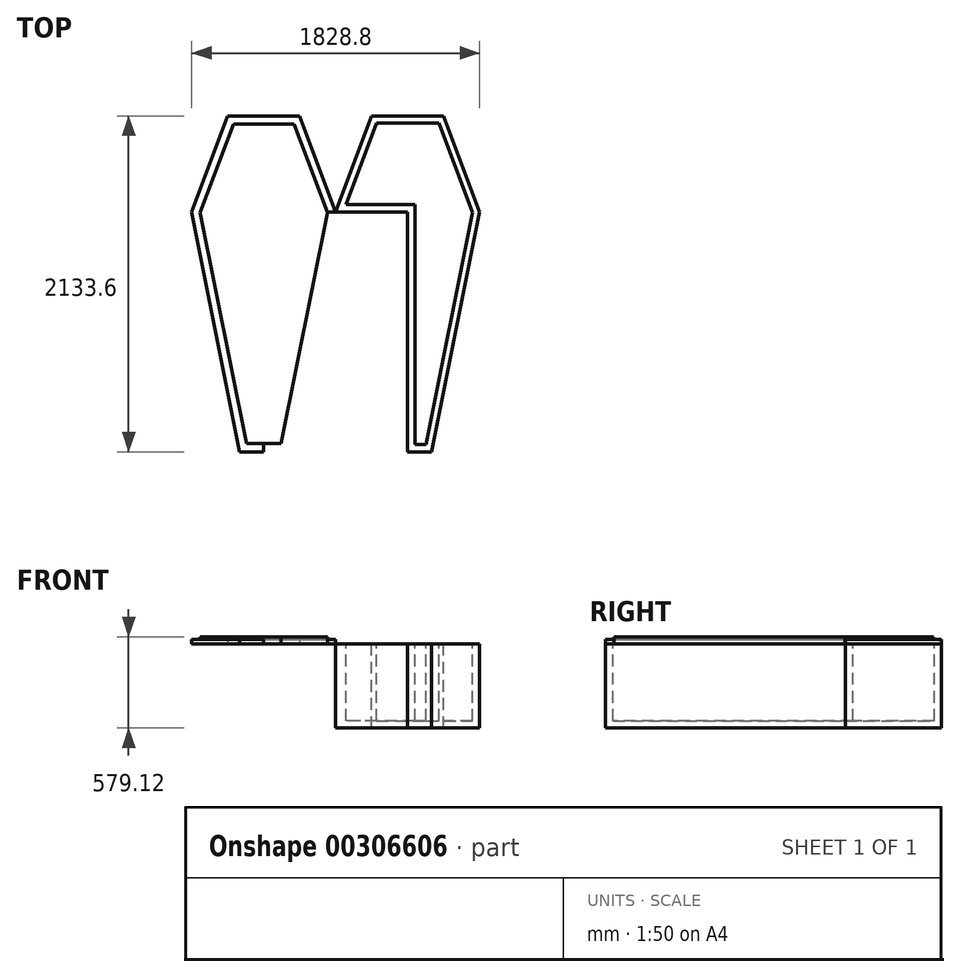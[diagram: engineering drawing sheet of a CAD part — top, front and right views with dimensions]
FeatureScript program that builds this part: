
annotation { "Feature Type Name" : "Feature", "Feature Type Description" : "" }
export const myFeature = defineFeature(function(context is Context, id is Id, definition is map)
    precondition{}
    {
        {
            var Q0;
            Q0=qCreatedBy(makeId("Top.planeOp"),FACE);
            var sketch = newSketch(context, id + "F0", { "sketchPlane" : qUnion([Q0])});
            skLineSegment(sketch, "E0", {"start": v(0, 0) * mm, "end": v(0, 609.6) * mm});
            skLineSegment(sketch, "E1", {"start": v(0, 0) * mm, "end": v(0, -1524) * mm});
            skLineSegment(sketch, "E2", {"start": v(0, 0) * mm, "end": v(-457.2, 0) * mm});
            skLineSegment(sketch, "E3", {"start": v(0, 0) * mm, "end": v(457.2, 0) * mm});
            skLineSegment(sketch, "E4", {"start": v(0, -1524) * mm, "end": v(152.4, -1524) * mm});
            skLineSegment(sketch, "E5", {"start": v(152.4, -1524) * mm, "end": v(0, -1524) * mm});
            skLineSegment(sketch, "E6", {"start": v(-152.4, -1524) * mm, "end": v(-457.2, 0) * mm});
            skLineSegment(sketch, "E7", {"start": v(-457.2, 0) * mm, "end": v(-228.6, 609.6) * mm});
            skLineSegment(sketch, "E8", {"start": v(-228.6, 609.6) * mm, "end": v(0, 609.6) * mm});
            skLineSegment(sketch, "E9", {"start": v(228.6, 609.6) * mm, "end": v(457.2, 0) * mm});
            skLineSegment(sketch, "E10", {"start": v(152.4, -1524) * mm, "end": v(457.2, 0) * mm});
            skLineSegment(sketch, "E11", {"start": v(228.6, 609.6) * mm, "end": v(0, 609.6) * mm});
            skLineSegment(sketch, "E12", {"start": v(-152.4, -1524) * mm, "end": v(0, -1524) * mm});
            skLineSegment(sketch, "E13", {"start": v(457.2, -1524) * mm, "end": v(457.2, 692.27) * mm, "construction": true});
            skLineSegment(sketch, "E14.MirrorCS", {"start": v(914.4, -1524) * mm, "end": v(762, -1524) * mm});
            skLineSegment(sketch, "E15.MirrorCS", {"start": v(762, -1524) * mm, "end": v(914.4, -1524) * mm});
            skLineSegment(sketch, "E16.MirrorCS", {"start": v(1066.8, -1524) * mm, "end": v(914.4, -1524) * mm});
            skLineSegment(sketch, "E17.MirrorCS", {"start": v(914.4, 0) * mm, "end": v(914.4, 609.6) * mm});
            skLineSegment(sketch, "E18.MirrorCS", {"start": v(914.4, 0) * mm, "end": v(914.4, -1524) * mm});
            skLineSegment(sketch, "E19.MirrorCS", {"start": v(914.4, 0) * mm, "end": v(1371.6, 0) * mm});
            skLineSegment(sketch, "E20.MirrorCS", {"start": v(914.4, 0) * mm, "end": v(457.2, 0) * mm});
            skLineSegment(sketch, "E21.MirrorCS", {"start": v(685.8, 609.6) * mm, "end": v(457.2, 0) * mm});
            skLineSegment(sketch, "E22.MirrorCS", {"start": v(1143, 609.6) * mm, "end": v(914.4, 609.6) * mm});
            skLineSegment(sketch, "E23.MirrorCS", {"start": v(1371.6, 0) * mm, "end": v(1143, 609.6) * mm});
            skLineSegment(sketch, "E24.MirrorCS", {"start": v(762, -1524) * mm, "end": v(457.2, 0) * mm});
            skLineSegment(sketch, "E25.MirrorCS", {"start": v(1066.8, -1524) * mm, "end": v(1371.6, 0) * mm});
            skLineSegment(sketch, "E26.MirrorCS", {"start": v(685.8, 609.6) * mm, "end": v(914.4, 609.6) * mm});
            skLineSegment(sketch, "E27.0", {"start": v(-109.92, -1472.18) * mm, "end": v(-403.49, -4.34) * mm});
            skLineSegment(sketch, "E27.1", {"start": v(-109.92, -1472.18) * mm, "end": v(0, -1472.18) * mm});
            skLineSegment(sketch, "E27.2", {"start": v(-403.49, -4.34) * mm, "end": v(-192.7, 557.78) * mm});
            skLineSegment(sketch, "E27.3", {"start": v(109.92, -1472.18) * mm, "end": v(0, -1472.18) * mm});
            skLineSegment(sketch, "E27.4", {"start": v(-192.7, 557.78) * mm, "end": v(0, 557.78) * mm});
            skLineSegment(sketch, "E27.5", {"start": v(192.7, 557.78) * mm, "end": v(0, 557.78) * mm});
            skLineSegment(sketch, "E27.6", {"start": v(192.7, 557.78) * mm, "end": v(403.49, -4.34) * mm});
            skLineSegment(sketch, "E27.7", {"start": v(109.92, -1472.18) * mm, "end": v(403.49, -4.34) * mm});
            skSolve(sketch);
        }
        {
            var Q0;
            Q0=makeQuery(id+"F0.imprint","IMPRINT",FACE,{"disambiguationData":[TD([[makeQuery(id+"F0.imprint","IMPRINT",EDGE,{"derivedFrom":sQuery(id+"F0.wireOp",EDGE,"E0")}),1.0]])]});
            var Q1;
            Q1=makeQuery(id+"F0.imprint","IMPRINT",FACE,{"disambiguationData":[TD([[makeQuery(id+"F0.imprint","IMPRINT",EDGE,{"derivedFrom":sQuery(id+"F0.wireOp",EDGE,"E0")}),-1.0]])]});
            var Q2;
            Q2=makeQuery(id+"F0.imprint","IMPRINT",FACE,{"disambiguationData":[TD([[makeQuery(id+"F0.imprint","IMPRINT",EDGE,{"derivedFrom":sQuery(id+"F0.wireOp",EDGE,"E1")}),1.0]])]});
            var Q3;
            Q3=makeQuery(id+"F0.imprint","IMPRINT",FACE,{"disambiguationData":[TD([[makeQuery(id+"F0.imprint","IMPRINT",EDGE,{"derivedFrom":sQuery(id+"F0.wireOp",EDGE,"E1")}),-1.0]])]});
            extrude(context, id + "F1", {"entities" : qUnion([Q0, Q1, Q2, Q3]), "depth" : 45.72 * mm});
        }
        {
            var Q0;
            Q0=makeQuery(id+"F0.imprint","IMPRINT",FACE,{"disambiguationData":[TD([[makeQuery(id+"F0.imprint","IMPRINT",EDGE,{"derivedFrom":sQuery(id+"F0.wireOp",EDGE,"E17.MirrorCS")}),1.0]])]});
            var Q1;
            Q1=makeQuery(id+"F0.imprint","IMPRINT",FACE,{"disambiguationData":[TD([[makeQuery(id+"F0.imprint","IMPRINT",EDGE,{"derivedFrom":sQuery(id+"F0.wireOp",EDGE,"E17.MirrorCS")}),-1.0]])]});
            var Q2;
            Q2=makeQuery(id+"F0.imprint","IMPRINT",FACE,{"disambiguationData":[TD([[makeQuery(id+"F0.imprint","IMPRINT",EDGE,{"derivedFrom":sQuery(id+"F0.wireOp",EDGE,"E16.MirrorCS")}),-1.0]])]});
            var Q3;
            Q3=makeQuery(id+"F0.imprint","IMPRINT",FACE,{"disambiguationData":[TD([[makeQuery(id+"F0.imprint","IMPRINT",EDGE,{"derivedFrom":sQuery(id+"F0.wireOp",EDGE,"E15.MirrorCS")}),1.0]])]});
            extrude(context, id + "F2", {"entities" : qUnion([Q0, Q1, Q2, Q3]), "oppositeDirection" : true, "depth" : 533.4 * mm});
        }
        {
            var Q0;
            Q0=makeQuery(id+"F2.opExtrude","CAP_FACE",FACE,{"disambiguationData":[OSD([sQuery(id+"F0.wireOp",EDGE,"E15.MirrorCS"),sQuery(id+"F0.wireOp",EDGE,"E16.MirrorCS"),sQuery(id+"F0.wireOp",EDGE,"E21.MirrorCS"),sQuery(id+"F0.wireOp",EDGE,"E22.MirrorCS"),sQuery(id+"F0.wireOp",EDGE,"E23.MirrorCS"),sQuery(id+"F0.wireOp",EDGE,"E24.MirrorCS"),sQuery(id+"F0.wireOp",EDGE,"E25.MirrorCS"),sQuery(id+"F0.wireOp",EDGE,"E26.MirrorCS")])],"isStart":true});
            shell(context, id + "F3", {"entities" : qUnion([Q0]), "thickness" : 45.72 * mm});
        }
        {
            var Q0;
            {var subQ0=sQuery(id+"F0.wireOp",EDGE,"E7");Q0=makeQuery(id+"F0.imprint","IMPRINT",FACE,{"disambiguationData":[TD([[makeQuery(id+"F0.imprint","IMPRINT",EDGE,{"derivedFrom":subQ0}),-1.0]])]});}
            var Q1;
            {var subQ0=sQuery(id+"F0.wireOp",EDGE,"E6");Q1=makeQuery(id+"F0.imprint","IMPRINT",FACE,{"disambiguationData":[TD([[makeQuery(id+"F0.imprint","IMPRINT",EDGE,{"derivedFrom":subQ0}),-1.0]])]});}
            var Q2;
            {var subQ4=sQuery(id+"F0.wireOp",EDGE,"E5");Q2=makeQuery(id+"F0.imprint","IMPRINT",FACE,{"disambiguationData":[TD([[makeQuery(id+"F0.imprint","IMPRINT",EDGE,{"derivedFrom":subQ4}),-1.0]])]});}
            var Q3;
            {var subQ1=sQuery(id+"F0.wireOp",EDGE,"E9");Q3=makeQuery(id+"F0.imprint","IMPRINT",FACE,{"disambiguationData":[TD([[makeQuery(id+"F0.imprint","IMPRINT",EDGE,{"derivedFrom":subQ1}),-1.0]])]});}
            extrude(context, id + "F4", {"entities" : qUnion([Q0, Q1, Q2, Q3]), "operationType" : NewBodyOperationType.ADD, "depth" : 30.48 * mm});
        }
    });
